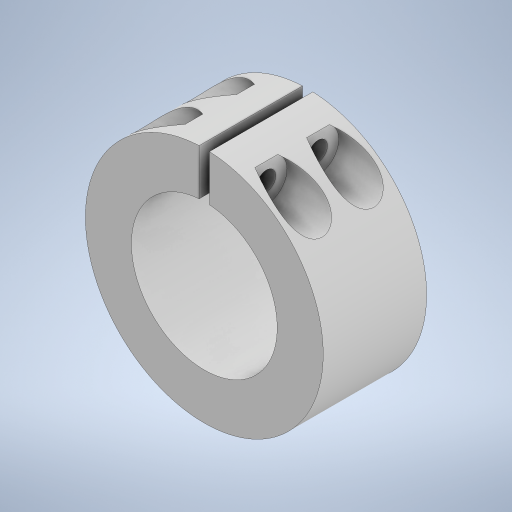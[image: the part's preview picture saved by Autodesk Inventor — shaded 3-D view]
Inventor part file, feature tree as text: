
AUTODESK INVENTOR PART (.ipt)
format: ipt  version: 2023 (Build 270158000, 158)  size: 342,528 bytes
history: native  units: mm
features: sketch x7, hole x5, extrude x2, plane x2, projected_geometry x2
ambient origin geometry x8: Origin, YZ Plane, XZ Plane, XY Plane, X Axis, Y Axis, Z Axis, Center Point
bodies: Solid1 (feature_tree)
feature tree (18):
  extrude  "Extrusion1"  Depth=92.0mm
  hole  "Hole1"  [1 undecoded]
  extrude  "Extrusion2"  TaperAngle=30.0deg  [1 undecoded]
  hole  "Hole2"  [1 undecoded]
  hole  "Hole3"  [1 undecoded]
  plane  "Work Plane1"
  hole  "Hole4"  [1 undecoded]
  plane  "Work Plane2"
  hole  "Hole5"  [1 undecoded]
  sketch  "Sketch1"  dims[d0=56.4mm d1=92.0mm]
  sketch  "Sketch2"  dims[d2=40.0mm d3=0.0mm d4=30.0deg]
  sketch  "Sketch3"  dims[d5=30.0deg d6=30.0deg]
  projected_geometry  "Projected Loop1"
  sketch  "Sketch4"  dims[d7=30.0deg d8=62.0mm]
  projected_geometry  "Projected Loop2"
  sketch  "Sketch5"  dims[d9=80.0mm]
  sketch  "Sketch6"  dims[d10=2.85mm d11=6.0mm d12=7.2mm d13=4.4mm d14=90.0deg d15=8.0mm d16=0.0mm d17=4.0mm]
  sketch  "Sketch7"  dims[d18=25.0mm d19=50.0mm d20=0.0mm d21=0.0mm d22=9.0mm d23=9.0mm d24=10.0mm d25=10.0mm d26=7.3mm d27=6.0mm d28=4.0mm d29=2.0mm d30=90.0deg d31=8.0mm d32=0.0mm d33=6.2mm d34=6.0mm d35=4.0mm d36=2.0mm d37=90.0deg d38=8.0mm d39=0.0mm d40=-35.0mm d41=16.0mm d42=6.0mm d43=4.0mm d44=2.0mm d45=90.0deg d46=23.0mm d47=0.0mm d48=-35.0mm d49=15.0mm d50=6.0mm d51=4.0mm d52=2.0mm d53=90.0deg d54=23.0mm d55=0.0mm]
note: 6 required parameter values undecoded (feature->parameter linkage not recoverable at this tier; creation-order binding heuristic only, values carry confidence <= 0.55)
